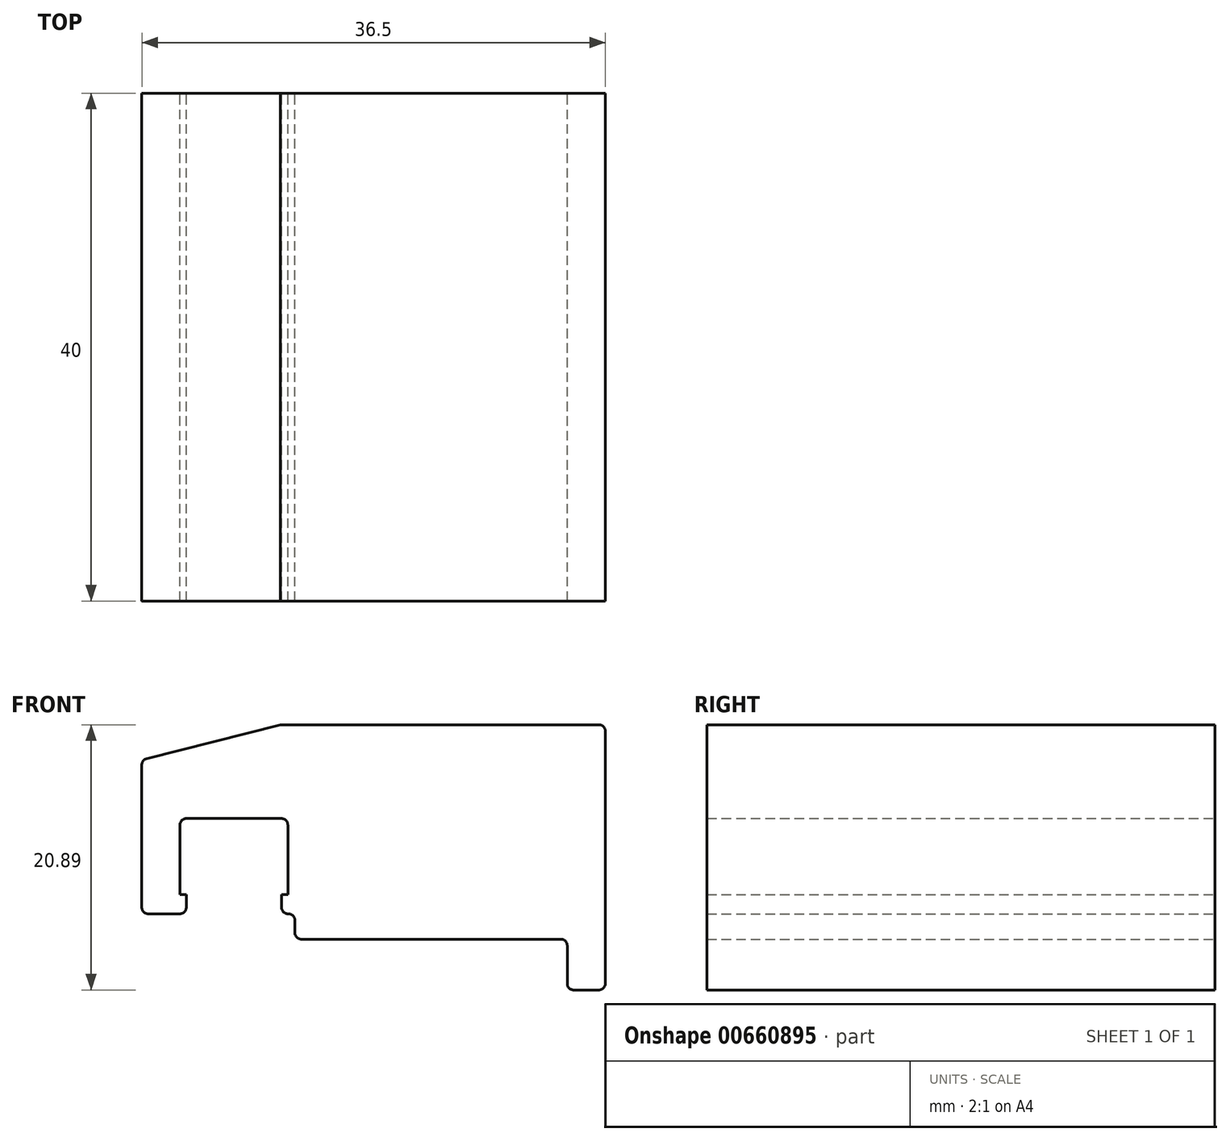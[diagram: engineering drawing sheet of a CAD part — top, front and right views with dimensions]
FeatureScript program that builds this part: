
annotation { "Feature Type Name" : "Feature", "Feature Type Description" : "" }
export const myFeature = defineFeature(function(context is Context, id is Id, definition is map)
    precondition{}
    {
        {
            var Q0;
            Q0=qCreatedBy(makeId("Front.planeOp"),FACE);
            var sketch = newSketch(context, id + "F0", { "sketchPlane" : qUnion([Q0])});
            skLineSegment(sketch, "E0", {"start": v(-9.5, 13.4) * mm, "end": v(-20.4, 10.63) * mm});
            skLineSegment(sketch, "E1", {"start": v(-9.5, 13.4) * mm, "end": v(16.1, 13.4) * mm});
            skLineSegment(sketch, "E2", {"start": v(16.1, 13.4) * mm, "end": v(16.1, -7.5) * mm});
            skLineSegment(sketch, "E3", {"start": v(16.1, -7.5) * mm, "end": v(13.1, -7.5) * mm});
            skLineSegment(sketch, "E4", {"start": v(13.1, -7.5) * mm, "end": v(13.1, -3.5) * mm});
            skLineSegment(sketch, "E5", {"start": v(13.1, -3.5) * mm, "end": v(-8.34, -3.5) * mm});
            skLineSegment(sketch, "E6", {"start": v(-8.34, -3.5) * mm, "end": v(-8.34, -1.5) * mm});
            skLineSegment(sketch, "E7", {"start": v(-8.9, 6) * mm, "end": v(-17.4, 6) * mm});
            skLineSegment(sketch, "E8", {"start": v(-17.4, 6) * mm, "end": v(-17.4, 0) * mm});
            skLineSegment(sketch, "E9", {"start": v(-17.4, 0) * mm, "end": v(-16.9, 0) * mm});
            skLineSegment(sketch, "E10", {"start": v(-16.9, 0) * mm, "end": v(-16.9, -1.5) * mm});
            skLineSegment(sketch, "E11", {"start": v(-16.9, -1.5) * mm, "end": v(-20.4, -1.5) * mm});
            skLineSegment(sketch, "E12", {"start": v(-20.4, 10.63) * mm, "end": v(-20.4, -1.5) * mm});
            skLineSegment(sketch, "E13", {"start": v(-8.9, 6) * mm, "end": v(-8.9, 0) * mm});
            skLineSegment(sketch, "E14", {"start": v(-8.9, 0) * mm, "end": v(-9.4, 0) * mm});
            skLineSegment(sketch, "E15", {"start": v(-9.4, 0) * mm, "end": v(-9.4, -1.5) * mm});
            skLineSegment(sketch, "E16", {"start": v(-9.4, -1.5) * mm, "end": v(-8.34, -1.5) * mm});
            skSolve(sketch);
        }
        {
            var Q0;
            Q0=makeQuery(id+"F0.imprint","IMPRINT",FACE,{"disambiguationData":[TD([[makeQuery(id+"F0.imprint","IMPRINT",EDGE,{"derivedFrom":sQuery(id+"F0.wireOp",EDGE,"E0")}),1.0]])]});
            extrude(context, id + "F1", {"entities" : qUnion([Q0]), "depth" : 40 * mm, "offsetDistance" : 25 * mm});
        }
        {
            var Q0;
            Q0=makeQuery(id+"F1.opExtrude","SWEPT_EDGE",EDGE,{"disambiguationData":[OSD([sQuery(id+"F0.wireOp",EDGE,"E10"),sQuery(id+"F0.wireOp",EDGE,"E11")])]});
            var Q1;
            Q1=makeQuery(id+"F1.opExtrude","SWEPT_EDGE",EDGE,{"disambiguationData":[OSD([sQuery(id+"F0.wireOp",EDGE,"E5"),sQuery(id+"F0.wireOp",EDGE,"E6")])]});
            var Q2;
            Q2=makeQuery(id+"F1.opExtrude","SWEPT_EDGE",EDGE,{"disambiguationData":[OSD([sQuery(id+"F0.wireOp",EDGE,"E3"),sQuery(id+"F0.wireOp",EDGE,"E4")])]});
            var Q3;
            Q3=makeQuery(id+"F1.opExtrude","SWEPT_EDGE",EDGE,{"disambiguationData":[OSD([sQuery(id+"F0.wireOp",EDGE,"E2"),sQuery(id+"F0.wireOp",EDGE,"E3")])]});
            var Q4;
            Q4=makeQuery(id+"F1.opExtrude","SWEPT_EDGE",EDGE,{"disambiguationData":[OSD([sQuery(id+"F0.wireOp",EDGE,"E1"),sQuery(id+"F0.wireOp",EDGE,"E2")])]});
            var Q5;
            Q5=makeQuery(id+"F1.opExtrude","SWEPT_EDGE",EDGE,{"disambiguationData":[OSD([sQuery(id+"F0.wireOp",EDGE,"E11"),sQuery(id+"F0.wireOp",EDGE,"E12")])]});
            var Q6;
            Q6=makeQuery(id+"F1.opExtrude","SWEPT_EDGE",EDGE,{"disambiguationData":[OSD([sQuery(id+"F0.wireOp",EDGE,"E0"),sQuery(id+"F0.wireOp",EDGE,"E12")])]});
            var Q7;
            Q7=makeQuery(id+"F1.opExtrude","SWEPT_EDGE",EDGE,{"disambiguationData":[OSD([sQuery(id+"F0.wireOp",EDGE,"E7"),sQuery(id+"F0.wireOp",EDGE,"E8")])]});
            var Q8;
            Q8=makeQuery(id+"F1.opExtrude","SWEPT_EDGE",EDGE,{"disambiguationData":[OSD([sQuery(id+"F0.wireOp",EDGE,"E7"),sQuery(id+"F0.wireOp",EDGE,"E13")])]});
            var Q9;
            Q9=makeQuery(id+"F1.opExtrude","SWEPT_EDGE",EDGE,{"disambiguationData":[OSD([sQuery(id+"F0.wireOp",EDGE,"E4"),sQuery(id+"F0.wireOp",EDGE,"E5")])]});
            var Q10;
            Q10=makeQuery(id+"F1.opExtrude","SWEPT_EDGE",EDGE,{"disambiguationData":[OSD([sQuery(id+"F0.wireOp",EDGE,"E6"),sQuery(id+"F0.wireOp",EDGE,"E16")])]});
            var Q11;
            Q11=makeQuery(id+"F1.opExtrude","SWEPT_EDGE",EDGE,{"disambiguationData":[OSD([sQuery(id+"F0.wireOp",EDGE,"E15"),sQuery(id+"F0.wireOp",EDGE,"E16")])]});
            fillet(context, id + "F2", {"entities" : qUnion([Q0, Q1, Q2, Q3, Q4, Q5, Q6, Q7, Q8, Q9, Q10, Q11]), "radius" : .5 * mm, "tangentPropagation" : true, "allowEdgeOverflow" : false});
        }
    });
